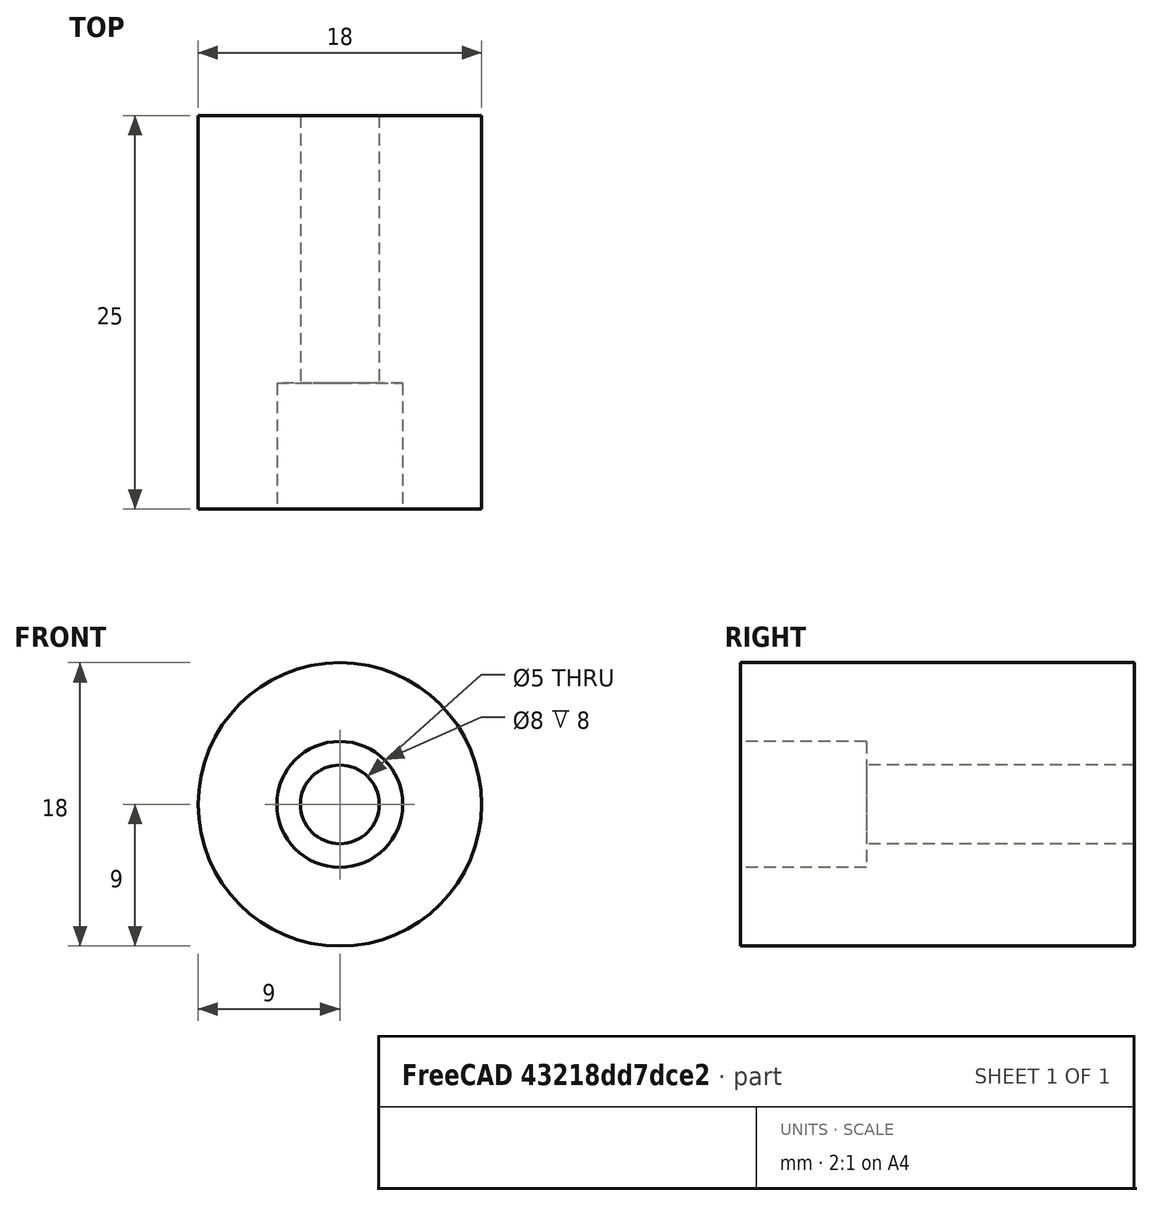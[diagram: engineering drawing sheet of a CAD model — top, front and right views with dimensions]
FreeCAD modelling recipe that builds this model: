
FCSTD DOCUMENT  (FreeCAD 0.15R4671 (Git))
Label: Accouplement
License: All rights reserved
LicenseURL: http://en.wikipedia.org/wiki/All_rights_reserved
objects: Sketcher::SketchObject×1, PartDesign::Revolution×1
note: 3 computed .brp shape members not serialized (recipe doc carries the construction recipe); baked Part::Feature solids carry a one-line shape summary decoded from their .brp

FEATURE [Sketcher::SketchObject] Sketch
  Placement = pos=(0,0,0) rot=(0.57735,0.57735,0.57735;2.0944rad)
  sketch-geometry (6):
    g0: LineSegment StartX=0 StartY=2.5 StartZ=0 EndX=-17 EndY=2.5 EndZ=0
    g1: LineSegment StartX=-17 StartY=2.5 StartZ=0 EndX=-17 EndY=4 EndZ=0
    g2: LineSegment StartX=-17 StartY=4 StartZ=0 EndX=-25 EndY=4 EndZ=0
    g3: LineSegment StartX=-25 StartY=4 StartZ=0 EndX=-25 EndY=9 EndZ=0
    g4: LineSegment StartX=-25 StartY=9 StartZ=0 EndX=0 EndY=9 EndZ=0
    g5: LineSegment StartX=0 StartY=9 StartZ=0 EndX=0 EndY=2.5 EndZ=0
  constraints (18):
    c: PointOnObject(g0,g-2)
    c: Horizontal(g0)
    c: Coincident(g0,g1)
    c: Vertical(g1)
    c: Coincident(g1,g2)
    c: Horizontal(g2)
    c: Coincident(g2,g3)
    c: Vertical(g3)
    c: Coincident(g3,g4)
    c: PointOnObject(g4,g-2)
    c: Horizontal(g4)
    c: Coincident(g4,g5)
    c: Coincident(g5,g0)
    c: DistanceY(g-1,g4) = 9
    c: DistanceY(g-1,g0) = 2.5
    c: DistanceY(g-1,g2) = 4
    c: DistanceX(g4) = 25
    c: Distance(g2) = 8
FEATURE [PartDesign::Revolution] Revolution
  Angle = 360
  Axis = (0,1,0)
  Base = (0,0,0)
  Placement = pos=(0,0,0) rot=(0.57735,0.57735,0.57735;2.0944rad)
  ReferenceAxis = -> Sketch [H_Axis]
  Sketch = -> Sketch
